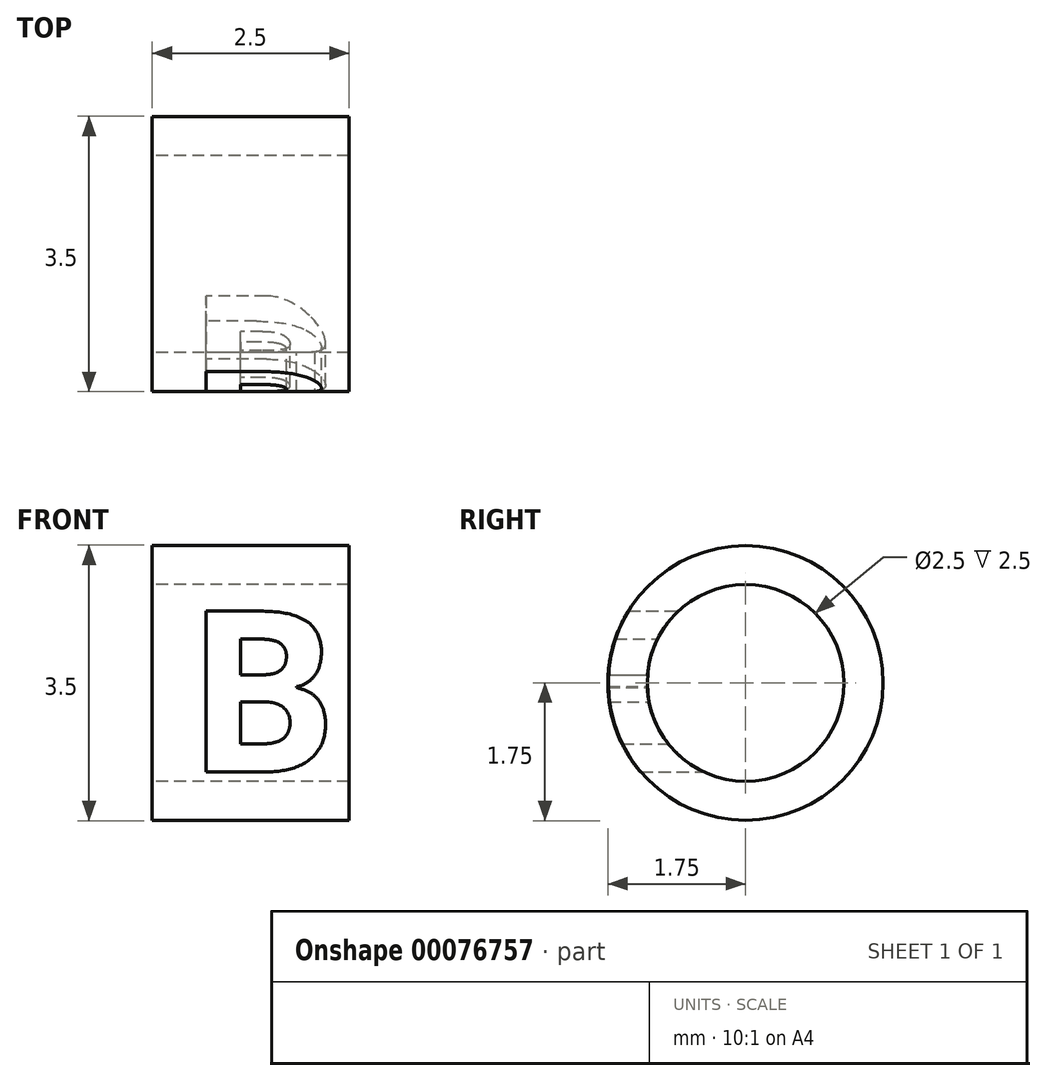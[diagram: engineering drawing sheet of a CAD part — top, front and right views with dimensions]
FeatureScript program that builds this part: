
annotation { "Feature Type Name" : "Feature", "Feature Type Description" : "" }
export const myFeature = defineFeature(function(context is Context, id is Id, definition is map)
    precondition{}
    {
        {
            var Q0;
            Q0=qCreatedBy(makeId("Right.planeOp"),FACE);
            var sketch = newSketch(context, id + "F0", { "sketchPlane" : qUnion([Q0])});
            skCircle(sketch, "E0", {"center": v(0, 0) * mm, "radius": 1.25 * mm});
            skCircle(sketch, "E1", {"center": v(0, 0) * mm, "radius": 1.75 * mm});
            skSolve(sketch);
        }
        {
            var Q0;
            Q0=makeQuery(id+"F0.imprint","IMPRINT",FACE,{"disambiguationData":[TD([[makeQuery(id+"F0.imprint","IMPRINT",EDGE,{"derivedFrom":sQuery(id+"F0.wireOp",EDGE,"E0")}),-1.0]])]});
            var Q1;
            Q1=makeQuery(id+"F0.imprint","IMPRINT",FACE,{"disambiguationData":[TD([[makeQuery(id+"F0.imprint","IMPRINT",EDGE,{"derivedFrom":sQuery(id+"F0.wireOp",EDGE,"E1")}),1.0]])]});
            extrude(context, id + "F1", {"entities" : qUnion([Q0, Q1]), "depth" : 2.5 * mm});
        }
        {
            var Q0;
            Q0=qCreatedBy(makeId("Front.planeOp"),FACE);
            var sketch = newSketch(context, id + "F2", { "sketchPlane" : qUnion([Q0])});
            skText(sketch, "E2", { "text": "B", "fontName": "OpenSans-Bold.ttf"});
            const initialGuessF2  = {"E2": [0.00043, -0.00113, 1, 0, 0.00206]};
            skSetInitialGuess(sketch, initialGuessF2);
            skSolve(sketch);
        }
        {
            var Q0;
            Q0=qSketchRegion(id+"F2",true);
            var Q1;
            Q1=qConstructionFilter(qBodyType(qCreatedBy(id+"F2",EDGE),BodyType.WIRE),ConstructionObject.NO);
            var Q2;
            Q2=makeQuery(id+"F1.opExtrude","SWEPT_FACE",FACE,{"disambiguationData":[OSD([sQuery(id+"F0.wireOp",EDGE,"E1")])]});
            var Q3;
            Q3=makeQuery(id+"F1.opExtrude","SWEPT_BODY",BODY,{"disambiguationData":[OSD([sQuery(id+"F0.wireOp",EDGE,"E0"),sQuery(id+"F0.wireOp",EDGE,"E1")])]});
            var Q4;
            Q4=sQuery(id+"F0.wireOp",VERTEX,"27635d6e-dcd6-4653-b727-4819003c0945");
            extrude(context, id + "F3", {"entities" : qUnion([Q0]), "operationType" : NewBodyOperationType.INTERSECT, "surfaceEntities" : qUnion([Q1]), "endBound" : BoundingType.UP_TO_SURFACE, "endBoundEntityFace" : qUnion([Q2]), "endBoundEntityBody" : qUnion([Q3]), "endBoundEntityVertex" : qUnion([Q4]), "depth" : 25 * mm});
        }
        {
            var Q0;
            Q0=makeQuery(id+"F0.imprint","IMPRINT",FACE,{"disambiguationData":[TD([[makeQuery(id+"F0.imprint","IMPRINT",EDGE,{"derivedFrom":sQuery(id+"F0.wireOp",EDGE,"E0")}),-1.0]])]});
            extrude(context, id + "F4", {"entities" : qUnion([Q0]), "depth" : 2.5 * mm});
        }
    });
